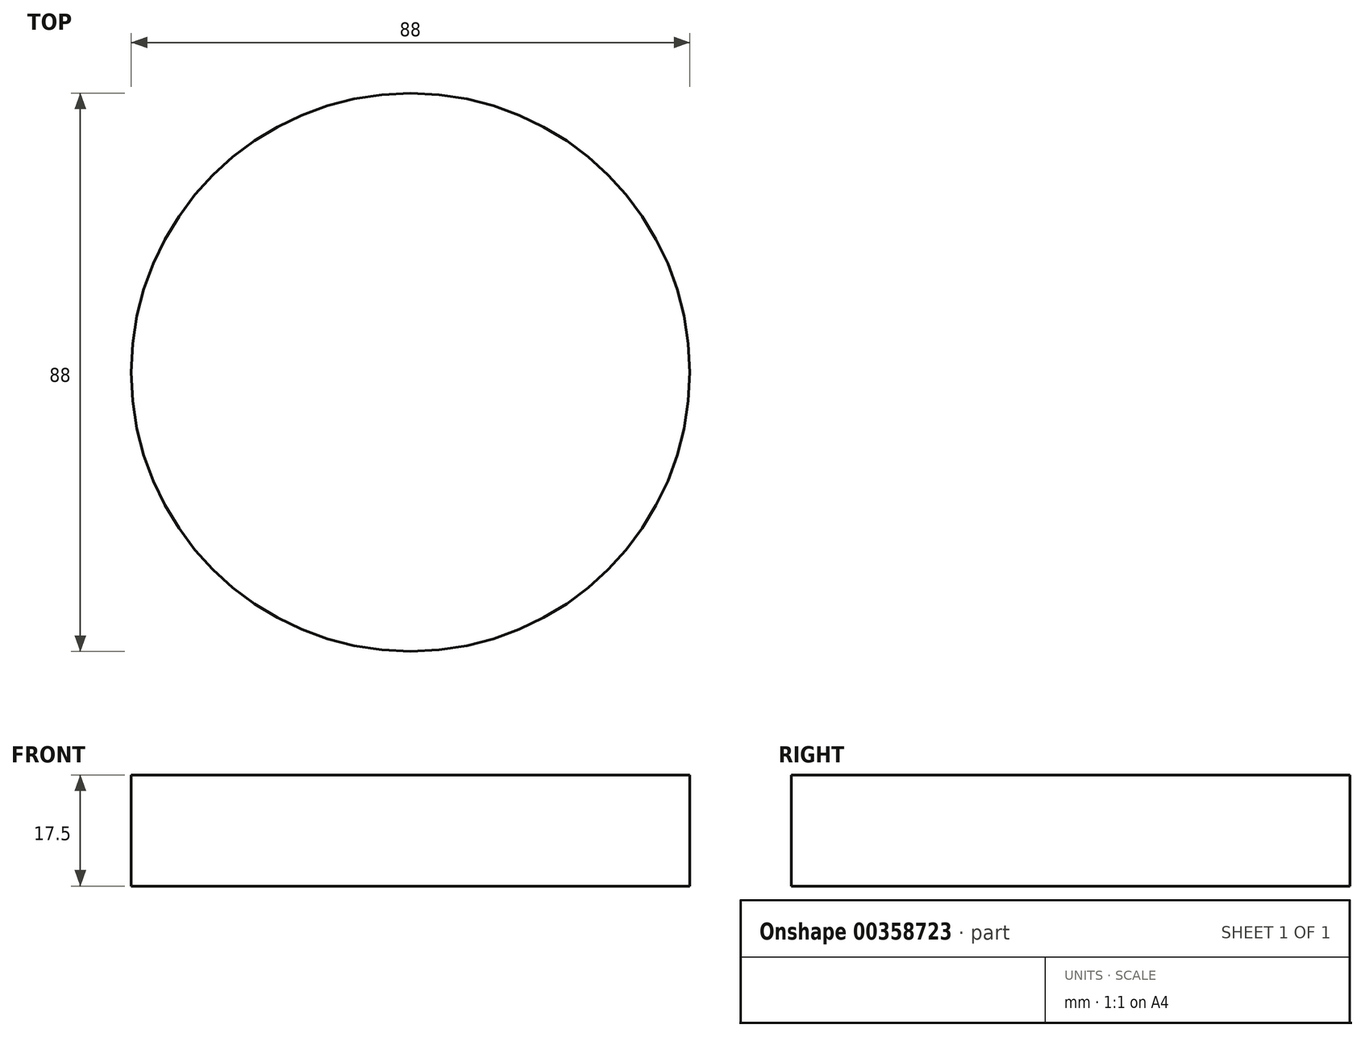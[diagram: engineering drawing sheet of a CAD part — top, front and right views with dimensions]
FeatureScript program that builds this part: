
annotation { "Feature Type Name" : "Feature", "Feature Type Description" : "" }
export const myFeature = defineFeature(function(context is Context, id is Id, definition is map)
    precondition{}
    {
        {
            var Q0;
            Q0=qCreatedBy(makeId("Top.planeOp"),FACE);
            var sketch = newSketch(context, id + "F0", { "sketchPlane" : qUnion([Q0])});
            skCircle(sketch, "E0", {"center": v(0, 0) * mm, "radius": 44 * mm});
            skSolve(sketch);
        }
        {
            var Q0;
            Q0 = qSketchRegion(id + "F0", true);
            extrude(context, id + "F1", {"entities" : qUnion([Q0]), "depth" : (14.8 + 2.7) * mm});
        }
    });
